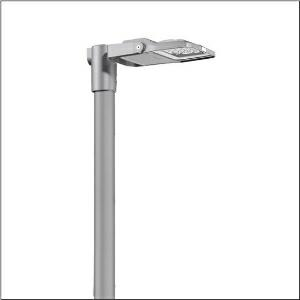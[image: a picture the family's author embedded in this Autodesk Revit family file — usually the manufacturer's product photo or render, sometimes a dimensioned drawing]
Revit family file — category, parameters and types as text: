
# Revit family: floodlight_fl_21_iq_micro___pl64_5xa7762a4e3a_dfd9
name_source: partatom
category: Lighting Fixtures
units: mm (PartAtom-declared; Revit-internal decimal feet)

## family parameters
Cut with Voids When Loaded = No
Host = Face
Light Source = No
Part Type = Normal
Room Calculation Point = No
Round Connector Dimension = Use Diameter
Shared = No

## types (1)
- --- (1 x LED, 2980 lm, 23.1 W, 4000K)
    Apparent Load = 23 VA
    CIE Flux Codes = 28 80 98 100 100
    Color Rendering = 70
    Color Temperature = 4000K
    Default Elevation = 1800 mm
    Description = Floodlight FL 21 iQ micro, floodlight, primary light control with lens, of PMMA, primary optical cover: protective disc, of toughened safety glass, transparent, light distribution: PL64, light emission: direct distribution, installation type: surface-mounted, LED, High Power LED, rated luminous flux: 2.980lm, luminous efficacy: 129lm/W, light colour: 740, colour temperature: 4000K, control gear: iQ Street-Remote/DALI, control: Auto-Match, Temp-Guard, Night-Set, Smart-Wire, Desk-Remote (wireless, voltage-free reading and setting of iQ features in the workshop via application-optimized NFC function/RFID function), optimised constant luminous flux control (CLO 2.0), Street-Remote, with terminal, 6-pole, mains connection: 220..240V, AC, 50/60Hz, start of lifetime: 23W, end of service life: 24W, reduction: 11W, luminaire housing, of diecast aluminium, powder-coated, Siteco® metallic grey (DB 702S), corrosivity category C5 mid according to DIN EN ISO 12944, suitable for swimming pools, chlorine-resistant, sealing non-destructively replaceable, please order mast flange separately, mast bracket, of steel, galvanised, powder-coated, Siteco® metallic grey (DB 702S), protection rating (complete): IP66, insulation class (complete): insulation class II (safety insulation), certification: CE, ENEC, VDE, protection symbol: D, impact resistance: IK07, permissible operating ambient temperature: -40..+40°C, permissible operating ambient temperature for outdoor applications: -40..+50°C, standard: DIN EN 12944, LABS conformity tested according to VDMA 24364:2018-05, packaging unit: 1 piece

Light Distribution: PL64
    Height = 65 mm
    Lamp = 1 x LED
    Lamp Light Flux = 2980 lm
    Lamp Power = 23.1 W
    Lamp count = 1
    Length = 312 mm
    Luminous efficacy = 129 lm/W
    Manufacturer = Siteco
    ModVariant = No
    Model = 5XA7762A4E3A
    Number of Poles = 1
    OnlyDefault = Yes
    Power Factor = 1
    Product Name = Floodlight FL 21 iQ micro | PL64
    Product group = floodlight | pylon annexe
    ProductGroupID = 6200
    Protection Class = Protection class II
    Protection Degree = IP 66
    RLX_Detail_Level = 1
    RLX_Emergency_Light_Flux = 0 lm
    RLX_Emergency_Type = 0
    RLX_Emergency_Type_DB = No
    RlxData = <blob elided: 101773 chars, md5=0a46bee3>
    Socket = socket
    Standby Power = 0 W
    System Light Flux = 2980 lm
    System Power = 23 W
    Type Comments = factory setting: luminous flux: 100 % | dim-lin: 254 | 455 mA
    Type Image = l_1007121.jpg
    URL = http://relux.com
    VarID = @adj_180470
    Voltage = 0 V
    Weight = 0.00 kg
    Width = 230 mm

## geometry (parser evidence)
native form markers: Blend x4, Sweep x13
no freeform markers — native parametric forms only
